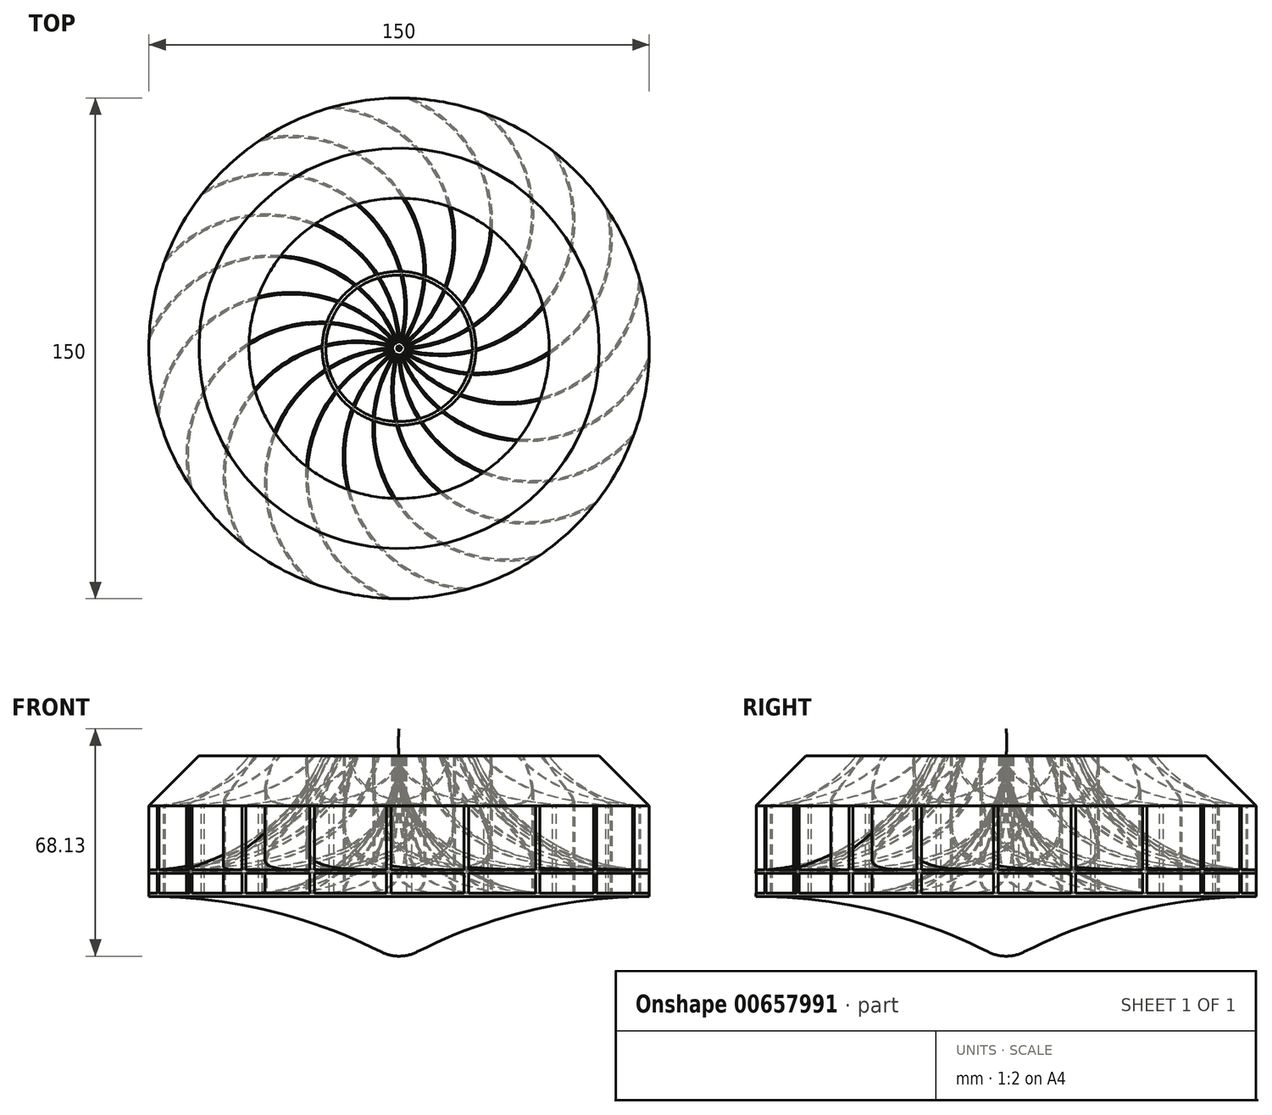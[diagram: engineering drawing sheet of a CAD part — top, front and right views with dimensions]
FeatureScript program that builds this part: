
annotation { "Feature Type Name" : "Feature", "Feature Type Description" : "" }
export const myFeature = defineFeature(function(context is Context, id is Id, definition is map)
    precondition{}
    {
        {
            assignVariable(context, id + "F0", {"name" : "d", "anyValue" : 150});
        }
        {
            var Q0;
            Q0=qCreatedBy(makeId("Top.planeOp"),FACE);
            var sketch = newSketch(context, id + "F1", { "sketchPlane" : qUnion([Q0])});
            skCircle(sketch, "E0", {"center": v(0, 0) * mm, "radius": 75 * mm, "construction": true});
            skCircle(sketch, "E1.0", {"center": v(0, 0) * mm, "radius": 80 * mm, "construction": true});
            skArc(sketch, "E2", {"start": v(0, 0) * mm, "mid": v(40, 40) * mm, "end": v(0, 80) * mm, "construction": true});
            skArc(sketch, "E3.0", {"start": v(0, -0.25) * mm, "mid": v(40.25, 40) * mm, "end": v(0, 80.25) * mm});
            skArc(sketch, "E4.0", {"start": v(0, 0.25) * mm, "mid": v(39.75, 40) * mm, "end": v(0, 79.75) * mm});
            skLineSegment(sketch, "E5", {"start": v(0, 80.25) * mm, "end": v(0, 79.75) * mm});
            skLineSegment(sketch, "E6", {"start": v(0, 0.25) * mm, "end": v(0, -0.25) * mm});
            skArc(sketch, "E7.1.0", {"start": v(-0.08, 0.24) * mm, "mid": v(25.44, 50.33) * mm, "end": v(-24.64, 75.85) * mm});
            skArc(sketch, "E7.1.1", {"start": v(0.08, -0.24) * mm, "mid": v(25.92, 50.48) * mm, "end": v(-24.8, 76.32) * mm});
            skLineSegment(sketch, "E7.1.2", {"start": v(-24.8, 76.32) * mm, "end": v(-24.64, 75.85) * mm});
            skLineSegment(sketch, "E7.1.3", {"start": v(-0.08, 0.24) * mm, "end": v(0.08, -0.24) * mm});
            skArc(sketch, "E8.2.2.0", {"start": v(-0.15, 0.2) * mm, "mid": v(8.65, 55.73) * mm, "end": v(-46.88, 64.52) * mm});
            skArc(sketch, "E8.4.2.0", {"start": v(0.15, -0.2) * mm, "mid": v(9.05, 56.02) * mm, "end": v(-47.17, 64.92) * mm});
            skLineSegment(sketch, "E8.8.2.0", {"start": v(-47.17, 64.92) * mm, "end": v(-46.88, 64.52) * mm});
            skLineSegment(sketch, "E8.11.2.0", {"start": v(-0.15, 0.2) * mm, "end": v(0.15, -0.2) * mm});
            skArc(sketch, "E8.2.3.0", {"start": v(-0.2, 0.15) * mm, "mid": v(-9, 55.67) * mm, "end": v(-64.52, 46.88) * mm});
            skArc(sketch, "E8.4.3.0", {"start": v(0.2, -0.15) * mm, "mid": v(-8.7, 56.07) * mm, "end": v(-64.92, 47.17) * mm});
            skLineSegment(sketch, "E8.8.3.0", {"start": v(-64.92, 47.17) * mm, "end": v(-64.52, 46.88) * mm});
            skLineSegment(sketch, "E8.11.3.0", {"start": v(-0.2, 0.15) * mm, "end": v(0.2, -0.15) * mm});
            skArc(sketch, "E8.2.4.0", {"start": v(-0.24, 0.08) * mm, "mid": v(-25.76, 50.17) * mm, "end": v(-75.85, 24.64) * mm});
            skArc(sketch, "E8.4.4.0", {"start": v(0.24, -0.08) * mm, "mid": v(-25.6, 50.64) * mm, "end": v(-76.32, 24.8) * mm});
            skLineSegment(sketch, "E8.8.4.0", {"start": v(-76.32, 24.8) * mm, "end": v(-75.85, 24.64) * mm});
            skLineSegment(sketch, "E8.11.4.0", {"start": v(-0.24, 0.08) * mm, "end": v(0.24, -0.08) * mm});
            skArc(sketch, "E8.2.5.0", {"start": v(-0.25, 0) * mm, "mid": v(-40, 39.75) * mm, "end": v(-79.75, 0) * mm});
            skArc(sketch, "E8.4.5.0", {"start": v(0.25, 0) * mm, "mid": v(-40, 40.25) * mm, "end": v(-80.25, 0) * mm});
            skLineSegment(sketch, "E8.8.5.0", {"start": v(-80.25, 0) * mm, "end": v(-79.75, 0) * mm});
            skLineSegment(sketch, "E8.11.5.0", {"start": v(-0.25, 0) * mm, "end": v(0.25, 0) * mm});
            skArc(sketch, "E8.2.6.0", {"start": v(-0.24, -0.08) * mm, "mid": v(-50.33, 25.44) * mm, "end": v(-75.85, -24.64) * mm});
            skArc(sketch, "E8.4.6.0", {"start": v(0.24, 0.08) * mm, "mid": v(-50.48, 25.92) * mm, "end": v(-76.32, -24.8) * mm});
            skLineSegment(sketch, "E8.8.6.0", {"start": v(-76.32, -24.8) * mm, "end": v(-75.85, -24.64) * mm});
            skLineSegment(sketch, "E8.11.6.0", {"start": v(-0.24, -0.08) * mm, "end": v(0.24, 0.08) * mm});
            skArc(sketch, "E8.2.7.0", {"start": v(-0.2, -0.15) * mm, "mid": v(-55.73, 8.65) * mm, "end": v(-64.52, -46.88) * mm});
            skArc(sketch, "E8.4.7.0", {"start": v(0.2, 0.15) * mm, "mid": v(-56.02, 9.05) * mm, "end": v(-64.92, -47.17) * mm});
            skLineSegment(sketch, "E8.8.7.0", {"start": v(-64.92, -47.17) * mm, "end": v(-64.52, -46.88) * mm});
            skLineSegment(sketch, "E8.11.7.0", {"start": v(-0.2, -0.15) * mm, "end": v(0.2, 0.15) * mm});
            skArc(sketch, "E8.2.8.0", {"start": v(-0.15, -0.2) * mm, "mid": v(-55.67, -9) * mm, "end": v(-46.88, -64.52) * mm});
            skArc(sketch, "E8.4.8.0", {"start": v(0.15, 0.2) * mm, "mid": v(-56.07, -8.7) * mm, "end": v(-47.17, -64.92) * mm});
            skLineSegment(sketch, "E8.8.8.0", {"start": v(-47.17, -64.92) * mm, "end": v(-46.88, -64.52) * mm});
            skLineSegment(sketch, "E8.11.8.0", {"start": v(-0.15, -0.2) * mm, "end": v(0.15, 0.2) * mm});
            skArc(sketch, "E8.2.9.0", {"start": v(-0.08, -0.24) * mm, "mid": v(-50.17, -25.76) * mm, "end": v(-24.64, -75.85) * mm});
            skArc(sketch, "E8.4.9.0", {"start": v(0.08, 0.24) * mm, "mid": v(-50.64, -25.6) * mm, "end": v(-24.8, -76.32) * mm});
            skLineSegment(sketch, "E8.8.9.0", {"start": v(-24.8, -76.32) * mm, "end": v(-24.64, -75.85) * mm});
            skLineSegment(sketch, "E8.11.9.0", {"start": v(-0.08, -0.24) * mm, "end": v(0.08, 0.24) * mm});
            skArc(sketch, "E8.2.10.0", {"start": v(0, -0.25) * mm, "mid": v(-39.75, -40) * mm, "end": v(0, -79.75) * mm});
            skArc(sketch, "E8.4.10.0", {"start": v(0, 0.25) * mm, "mid": v(-40.25, -40) * mm, "end": v(0, -80.25) * mm});
            skLineSegment(sketch, "E8.8.10.0", {"start": v(0, -80.25) * mm, "end": v(0, -79.75) * mm});
            skLineSegment(sketch, "E8.11.10.0", {"start": v(0, -0.25) * mm, "end": v(0, 0.25) * mm});
            skArc(sketch, "E8.2.11.0", {"start": v(0.08, -0.24) * mm, "mid": v(-25.44, -50.33) * mm, "end": v(24.64, -75.85) * mm});
            skArc(sketch, "E8.4.11.0", {"start": v(-0.08, 0.24) * mm, "mid": v(-25.92, -50.48) * mm, "end": v(24.8, -76.32) * mm});
            skLineSegment(sketch, "E8.8.11.0", {"start": v(24.8, -76.32) * mm, "end": v(24.64, -75.85) * mm});
            skLineSegment(sketch, "E8.11.11.0", {"start": v(0.08, -0.24) * mm, "end": v(-0.08, 0.24) * mm});
            skArc(sketch, "E8.2.12.0", {"start": v(0.15, -0.2) * mm, "mid": v(-8.65, -55.73) * mm, "end": v(46.88, -64.52) * mm});
            skArc(sketch, "E8.4.12.0", {"start": v(-0.15, 0.2) * mm, "mid": v(-9.05, -56.02) * mm, "end": v(47.17, -64.92) * mm});
            skLineSegment(sketch, "E8.8.12.0", {"start": v(47.17, -64.92) * mm, "end": v(46.88, -64.52) * mm});
            skLineSegment(sketch, "E8.11.12.0", {"start": v(0.15, -0.2) * mm, "end": v(-0.15, 0.2) * mm});
            skArc(sketch, "E8.2.13.0", {"start": v(0.2, -0.15) * mm, "mid": v(9, -55.67) * mm, "end": v(64.52, -46.88) * mm});
            skArc(sketch, "E8.4.13.0", {"start": v(-0.2, 0.15) * mm, "mid": v(8.7, -56.07) * mm, "end": v(64.92, -47.17) * mm});
            skLineSegment(sketch, "E8.8.13.0", {"start": v(64.92, -47.17) * mm, "end": v(64.52, -46.88) * mm});
            skLineSegment(sketch, "E8.11.13.0", {"start": v(0.2, -0.15) * mm, "end": v(-0.2, 0.15) * mm});
            skArc(sketch, "E8.2.14.0", {"start": v(0.24, -0.08) * mm, "mid": v(25.76, -50.17) * mm, "end": v(75.85, -24.64) * mm});
            skArc(sketch, "E8.4.14.0", {"start": v(-0.24, 0.08) * mm, "mid": v(25.6, -50.64) * mm, "end": v(76.32, -24.8) * mm});
            skLineSegment(sketch, "E8.8.14.0", {"start": v(76.32, -24.8) * mm, "end": v(75.85, -24.64) * mm});
            skLineSegment(sketch, "E8.11.14.0", {"start": v(0.24, -0.08) * mm, "end": v(-0.24, 0.08) * mm});
            skArc(sketch, "E8.2.15.0", {"start": v(0.25, 0) * mm, "mid": v(40, -39.75) * mm, "end": v(79.75, 0) * mm});
            skArc(sketch, "E8.4.15.0", {"start": v(-0.25, 0) * mm, "mid": v(40, -40.25) * mm, "end": v(80.25, 0) * mm});
            skLineSegment(sketch, "E8.8.15.0", {"start": v(80.25, 0) * mm, "end": v(79.75, 0) * mm});
            skLineSegment(sketch, "E8.11.15.0", {"start": v(0.25, 0) * mm, "end": v(-0.25, 0) * mm});
            skArc(sketch, "E8.2.16.0", {"start": v(0.24, 0.08) * mm, "mid": v(50.33, -25.44) * mm, "end": v(75.85, 24.64) * mm});
            skArc(sketch, "E8.4.16.0", {"start": v(-0.24, -0.08) * mm, "mid": v(50.48, -25.92) * mm, "end": v(76.32, 24.8) * mm});
            skLineSegment(sketch, "E8.8.16.0", {"start": v(76.32, 24.8) * mm, "end": v(75.85, 24.64) * mm});
            skLineSegment(sketch, "E8.11.16.0", {"start": v(0.24, 0.08) * mm, "end": v(-0.24, -0.08) * mm});
            skArc(sketch, "E8.2.17.0", {"start": v(0.2, 0.15) * mm, "mid": v(55.73, -8.65) * mm, "end": v(64.52, 46.88) * mm});
            skArc(sketch, "E8.4.17.0", {"start": v(-0.2, -0.15) * mm, "mid": v(56.02, -9.05) * mm, "end": v(64.92, 47.17) * mm});
            skLineSegment(sketch, "E8.8.17.0", {"start": v(64.92, 47.17) * mm, "end": v(64.52, 46.88) * mm});
            skLineSegment(sketch, "E8.11.17.0", {"start": v(0.2, 0.15) * mm, "end": v(-0.2, -0.15) * mm});
            skArc(sketch, "E8.2.18.0", {"start": v(0.15, 0.2) * mm, "mid": v(55.67, 9) * mm, "end": v(46.88, 64.52) * mm});
            skArc(sketch, "E8.4.18.0", {"start": v(-0.15, -0.2) * mm, "mid": v(56.07, 8.7) * mm, "end": v(47.17, 64.92) * mm});
            skLineSegment(sketch, "E8.8.18.0", {"start": v(47.17, 64.92) * mm, "end": v(46.88, 64.52) * mm});
            skLineSegment(sketch, "E8.11.18.0", {"start": v(0.15, 0.2) * mm, "end": v(-0.15, -0.2) * mm});
            skArc(sketch, "E8.2.19.0", {"start": v(0.08, 0.24) * mm, "mid": v(50.17, 25.76) * mm, "end": v(24.64, 75.85) * mm});
            skArc(sketch, "E8.4.19.0", {"start": v(-0.08, -0.24) * mm, "mid": v(50.64, 25.6) * mm, "end": v(24.8, 76.32) * mm});
            skLineSegment(sketch, "E8.8.19.0", {"start": v(24.8, 76.32) * mm, "end": v(24.64, 75.85) * mm});
            skLineSegment(sketch, "E8.11.19.0", {"start": v(0.08, 0.24) * mm, "end": v(-0.08, -0.24) * mm});
            skSolve(sketch);
        }
        {
            var Q0;
            Q0=qCreatedBy(makeId("Front.planeOp"),FACE);
            var sketch = newSketch(context, id + "F2", { "sketchPlane" : qUnion([Q0])});
            skLineSegment(sketch, "E9", {"start": v(0, 0) * mm, "end": v(-75, 0) * mm, "construction": true});
            skLineSegment(sketch, "E10", {"start": v(-75, 0) * mm, "end": v(-60, 15) * mm});
            skLineSegment(sketch, "E11", {"start": v(-60, 15) * mm, "end": v(-45, 15) * mm});
            skArc(sketch, "E12", {"start": v(-75, 0) * mm, "mid": v(-58.23, 3.96) * mm, "end": v(-45, 15) * mm});
            skArc(sketch, "E13", {"start": v(-75, -19.12) * mm, "mid": v(-43.92, -9.83) * mm, "end": v(-23.04, 15) * mm});
            skArc(sketch, "E14.0", {"start": v(-75, -20.12) * mm, "mid": v(-43.2, -10.54) * mm, "end": v(-21.96, 15) * mm});
            skLineSegment(sketch, "E15", {"start": v(-23.04, 15) * mm, "end": v(-21.96, 15) * mm});
            skLineSegment(sketch, "E16", {"start": v(-75, -19.12) * mm, "end": v(-75, -20.12) * mm});
            skLineSegment(sketch, "E17", {"start": v(-75, 0) * mm, "end": v(-75, -19.12) * mm});
            skLineSegment(sketch, "E18", {"start": v(-45, 15) * mm, "end": v(-23.04, 15) * mm});
            skLineSegment(sketch, "E19", {"start": v(-21.96, 15) * mm, "end": v(0, 15) * mm});
            skLineSegment(sketch, "E20", {"start": v(-75, -20.12) * mm, "end": v(-75, -26.12) * mm});
            skArc(sketch, "E21", {"start": v(-5.41, -43.7) * mm, "mid": v(-2.78, -44.67) * mm, "end": v(0, -45) * mm});
            skLineSegment(sketch, "E22", {"start": v(-75, -26.12) * mm, "end": v(-75, -27.12) * mm});
            skArc(sketch, "E23", {"start": v(-5.41, -43.7) * mm, "mid": v(-39.23, -31.32) * mm, "end": v(-75, -27.12) * mm});
            skLineSegment(sketch, "E24", {"start": v(0, 15) * mm, "end": v(0, -45) * mm});
            skLineSegment(sketch, "E25", {"start": v(-75, -26.12) * mm, "end": v(-45, -26.12) * mm});
            skLineSegment(sketch, "E26", {"start": v(-75, -27.12) * mm, "end": v(-75, -181.35) * mm, "construction": true});
            skArc(sketch, "E27", {"start": v(-45, -26.12) * mm, "mid": v(-14.52, -14.3) * mm, "end": v(0, 15) * mm});
            skSolve(sketch);
        }
        {
            var Q0;
            Q0=qCreatedBy(makeId("Front.planeOp"),FACE);
            var sketch = newSketch(context, id + "F3", { "sketchPlane" : qUnion([Q0])});
            skLineSegment(sketch, "E28", {"start": v(0, 54.47) * mm, "end": v(0, -63.51) * mm, "construction": true});
            skSolve(sketch);
        }
        {
            var Q0;
            Q0 = qSketchRegion(id + "F1", true);
            extrude(context, id + "F4", {"entities" : qUnion([Q0]), "endBound" : BoundingType.SYMMETRIC, "depth" : (getVariable(context, 'd')) * mm, "offsetDistance" : 25 * mm});
        }
        {
            var Q0;
            Q0=makeQuery(id+"F2.imprint","IMPRINT",FACE,{"disambiguationData":[TD([[makeQuery(id+"F2.imprint","IMPRINT",EDGE,{"derivedFrom":sQuery(id+"F2.wireOp",EDGE,"E10")}),-1.0]])]});
            var Q1;
            Q1=makeQuery(id+"F2.imprint","IMPRINT",FACE,{"disambiguationData":[TD([[makeQuery(id+"F2.imprint","IMPRINT",EDGE,{"derivedFrom":sQuery(id+"F2.wireOp",EDGE,"E13")}),-1.0]])]});
            var Q2;
            Q2=makeQuery(id+"F2.imprint","IMPRINT",FACE,{"disambiguationData":[TD([[makeQuery(id+"F2.imprint","IMPRINT",EDGE,{"derivedFrom":sQuery(id+"F2.wireOp",EDGE,"E21")}),1.0]])]});
            var Q3;
            Q3=sQuery(id+"F3.wireOp",EDGE,"E28");
            revolve(context, id + "F5", {"operationType" : NewBodyOperationType.ADD, "entities" : qUnion([Q0, Q1, Q2]), "axis" : qUnion([Q3]), "revolveType" : RevolveType.FULL});
        }
        {
            var Q0;
            Q0=makeQuery(id+"F2.imprint","IMPRINT",FACE,{"disambiguationData":[TD([[makeQuery(id+"F2.imprint","IMPRINT",EDGE,{"derivedFrom":sQuery(id+"F2.wireOp",EDGE,"E10")}),-1.0]])]});
            var Q1;
            Q1=makeQuery(id+"F2.imprint","IMPRINT",FACE,{"disambiguationData":[TD([[makeQuery(id+"F2.imprint","IMPRINT",EDGE,{"derivedFrom":sQuery(id+"F2.wireOp",EDGE,"E12")}),-1.0]])]});
            var Q2;
            Q2=makeQuery(id+"F2.imprint","IMPRINT",FACE,{"disambiguationData":[TD([[makeQuery(id+"F2.imprint","IMPRINT",EDGE,{"derivedFrom":sQuery(id+"F2.wireOp",EDGE,"E13")}),-1.0]])]});
            var Q3;
            Q3=makeQuery(id+"F2.imprint","IMPRINT",FACE,{"disambiguationData":[TD([[makeQuery(id+"F2.imprint","IMPRINT",EDGE,{"derivedFrom":sQuery(id+"F2.wireOp",EDGE,"E14.0")}),-1.0]])]});
            var Q4;
            Q4=makeQuery(id+"F2.imprint","IMPRINT",FACE,{"disambiguationData":[TD([[makeQuery(id+"F2.imprint","IMPRINT",EDGE,{"derivedFrom":sQuery(id+"F2.wireOp",EDGE,"E21")}),1.0]])]});
            var Q5;
            Q5=sQuery(id+"F3.wireOp",EDGE,"E28");
            revolve(context, id + "F6", {"operationType" : NewBodyOperationType.INTERSECT, "entities" : qUnion([Q0, Q1, Q2, Q3, Q4]), "axis" : qUnion([Q5]), "revolveType" : RevolveType.FULL});
        }
    });
